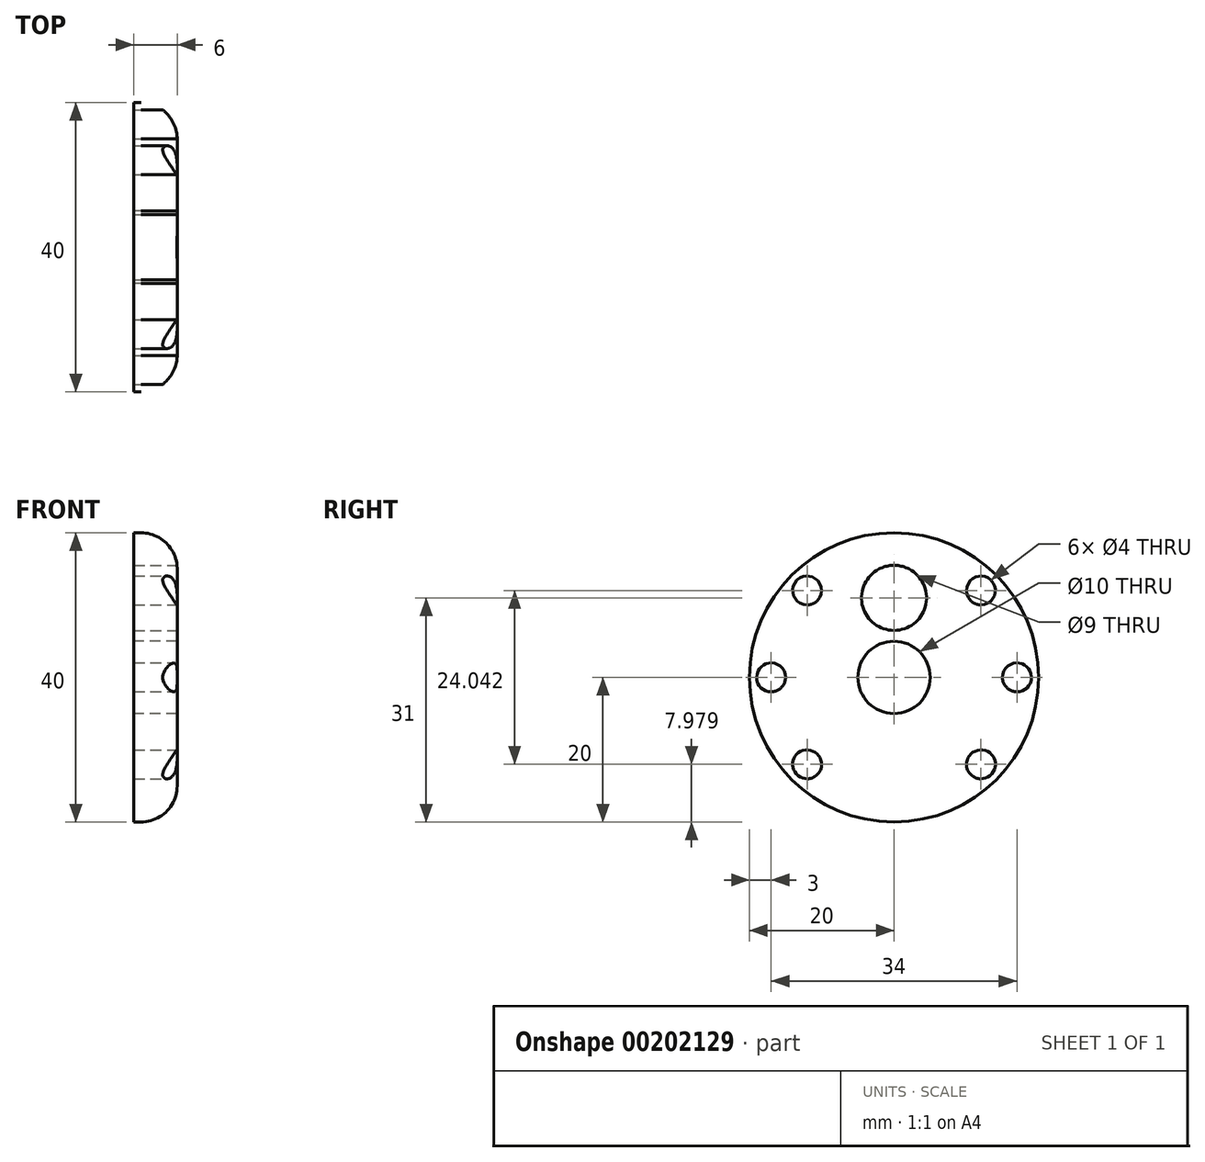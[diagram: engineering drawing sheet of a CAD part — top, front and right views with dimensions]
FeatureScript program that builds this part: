
annotation { "Feature Type Name" : "Feature", "Feature Type Description" : "" }
export const myFeature = defineFeature(function(context is Context, id is Id, definition is map)
    precondition{}
    {
        {
            var Q0;
            Q0=qCreatedBy(makeId("Right.planeOp"),FACE);
            var sketch = newSketch(context, id + "F0", { "sketchPlane" : qUnion([Q0])});
            skCircle(sketch, "E0", {"center": v(0, 0) * mm, "radius": 20 * mm});
            skCircle(sketch, "E1", {"center": v(0, 0) * mm, "radius": 5 * mm});
            skSolve(sketch);
        }
        {
            var Q0;
            Q0 = qSketchRegion(id + "F0", true);
            extrude(context, id + "F1", {"entities" : qUnion([Q0]), "depth" : 6 * mm});
        }
        {
            var Q0;
            Q0=makeQuery(id+"F1.opExtrude","CAP_FACE",FACE,{"disambiguationData":[OSD([sQuery(id+"F0.wireOp",EDGE,"E0"),sQuery(id+"F0.wireOp",EDGE,"E1")])],"isStart":false});
            var sketch = newSketch(context, id + "F2", { "sketchPlane" : qUnion([Q0])});
            skCircle(sketch, "E2", {"center": v(-17, 0) * mm, "radius": 2 * mm});
            skCircle(sketch, "E3.1.0", {"center": v(-12.02, 12.02) * mm, "radius": 2 * mm});
            skPoint(sketch, "E3.center", {"position": v(0, 0) * mm});
            skLineSegment(sketch, "E3.anchor1", {"start": v(0, 0) * mm, "end": v(-17, 0) * mm, "construction": true});
            skLineSegment(sketch, "E3.anchor2", {"start": v(0, 0) * mm, "end": v(17, 0) * mm, "construction": true});
            skCircle(sketch, "E4.1.3.0", {"center": v(12.02, 12.02) * mm, "radius": 2 * mm});
            skCircle(sketch, "E4.1.4.0", {"center": v(17, 0) * mm, "radius": 2 * mm});
            skCircle(sketch, "E5.MirrorC", {"center": v(-12.02, -12.02) * mm, "radius": 2 * mm});
            skCircle(sketch, "E6.MirrorC", {"center": v(12.02, -12.02) * mm, "radius": 2 * mm});
            skSolve(sketch);
        }
        {
            var Q0;
            Q0 = qSketchRegion(id + "F2", true);
            extrude(context, id + "F3", {"entities" : qUnion([Q0]), "operationType" : NewBodyOperationType.REMOVE, "endBound" : BoundingType.THROUGH_ALL, "oppositeDirection" : true, "depth" : 25 * mm});
        }
        {
            var Q0;
            Q0=makeQuery(id+"F1.opExtrude","CAP_FACE",FACE,{"disambiguationData":[OSD([sQuery(id+"F0.wireOp",EDGE,"E0"),sQuery(id+"F0.wireOp",EDGE,"E1")])],"isStart":false});
            var sketch = newSketch(context, id + "F4", { "sketchPlane" : qUnion([Q0])});
            skCircle(sketch, "E7", {"center": v(0, 11) * mm, "radius": 4.5 * mm});
            skSolve(sketch);
        }
        {
            var Q0;
            Q0 = qSketchRegion(id + "F4", true);
            extrude(context, id + "F5", {"entities" : qUnion([Q0]), "operationType" : NewBodyOperationType.REMOVE, "endBound" : BoundingType.THROUGH_ALL, "oppositeDirection" : true, "depth" : 25 * mm});
        }
        {
            var Q0;
            Q0=makeQuery(id+"F1.opExtrude","CAP_EDGE",EDGE,{"disambiguationData":[OSD([sQuery(id+"F0.wireOp",EDGE,"E0")])],"isStart":false});
            fillet(context, id + "F6", {"entities" : qUnion([Q0]), "radius" : 5 * mm, "tangentPropagation" : true, "allowEdgeOverflow" : false});
        }
    });
